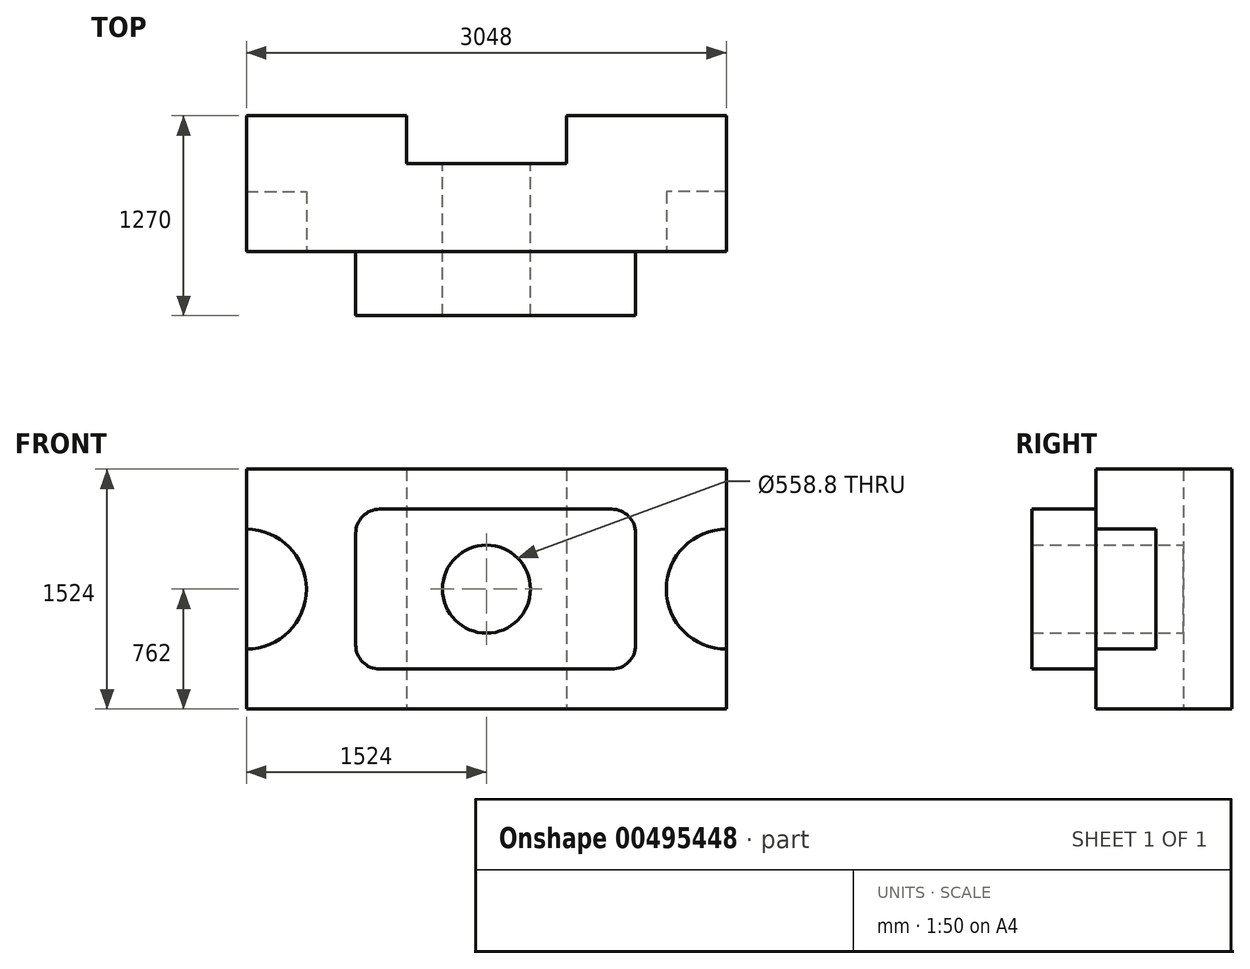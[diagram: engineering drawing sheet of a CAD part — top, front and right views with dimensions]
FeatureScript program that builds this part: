
annotation { "Feature Type Name" : "Feature", "Feature Type Description" : "" }
export const myFeature = defineFeature(function(context is Context, id is Id, definition is map)
    precondition{}
    {
        {
            var Q0;
            Q0=qCreatedBy(makeId("Front.planeOp"),FACE);
            var sketch = newSketch(context, id + "F0", { "sketchPlane" : qUnion([Q0])});
            skLineSegment(sketch, "E0.bottom", {"start": v(1524, -762) * mm, "end": v(-1524, -762) * mm});
            skLineSegment(sketch, "E0.top", {"start": v(1524, 762) * mm, "end": v(-1524, 762) * mm});
            skLineSegment(sketch, "E0.left", {"start": v(1524, -762) * mm, "end": v(1524, 762) * mm});
            skLineSegment(sketch, "E0.right", {"start": v(-1524, -762) * mm, "end": v(-1524, 762) * mm});
            skPoint(sketch, "E0.middle", {"position": v(0, 0) * mm});
            skSolve(sketch);
        }
        {
            var Q0;
            Q0=makeQuery(id+"F0.imprint","IMPRINT",FACE,{"disambiguationData":[TD([[makeQuery(id+"F0.imprint","IMPRINT",EDGE,{"derivedFrom":sQuery(id+"F0.wireOp",EDGE,"E0.bottom")}),-1.0]])]});
            extrude(context, id + "F1", {"entities" : qUnion([Q0]), "depth" : 863.6 * mm});
        }
        {
            var Q0;
            Q0=makeQuery(id+"F1.opExtrude","CAP_FACE",FACE,{"disambiguationData":[OSD([sQuery(id+"F0.wireOp",EDGE,"E0.bottom"),sQuery(id+"F0.wireOp",EDGE,"E0.top"),sQuery(id+"F0.wireOp",EDGE,"E0.left"),sQuery(id+"F0.wireOp",EDGE,"E0.right")])],"isStart":false});
            var sketch = newSketch(context, id + "F2", { "sketchPlane" : qUnion([Q0])});
            skArc(sketch, "E1", {"start": v(-1524, -381) * mm, "mid": v(-1143, 0) * mm, "end": v(-1524, 381) * mm});
            skArc(sketch, "E2", {"start": v(1524, 381) * mm, "mid": v(1143, 0) * mm, "end": v(1524, -381) * mm});
            skLineSegment(sketch, "E3", {"start": v(-1524, 381) * mm, "end": v(-1524, -381) * mm});
            skLineSegment(sketch, "E4", {"start": v(1524, 381) * mm, "end": v(1524, -381) * mm});
            skSolve(sketch);
        }
        {
            var Q0;
            Q0=makeQuery(id+"F2.imprint","IMPRINT",FACE,{"disambiguationData":[TD([[makeQuery(id+"F2.imprint","IMPRINT",EDGE,{"derivedFrom":sQuery(id+"F2.wireOp",EDGE,"E1")}),1.0]])]});
            var Q1;
            Q1=makeQuery(id+"F2.imprint","IMPRINT",FACE,{"disambiguationData":[TD([[makeQuery(id+"F2.imprint","IMPRINT",EDGE,{"derivedFrom":sQuery(id+"F2.wireOp",EDGE,"E2")}),1.0]])]});
            extrude(context, id + "F3", {"entities" : qUnion([Q0, Q1]), "operationType" : NewBodyOperationType.REMOVE, "oppositeDirection" : true, "depth" : 381 * mm});
        }
        {
            var Q0;
            Q0=makeQuery(id+"F1.opExtrude","SWEPT_FACE",FACE,{"disambiguationData":[OSD([sQuery(id+"F0.wireOp",EDGE,"E0.bottom")])]});
            var sketch = newSketch(context, id + "F4", { "sketchPlane" : qUnion([Q0])});
            skLineSegment(sketch, "E5.top", {"start": v(508, 304.8) * mm, "end": v(-508, 304.8) * mm});
            skLineSegment(sketch, "E5.left", {"start": v(508, 0) * mm, "end": v(508, 304.8) * mm});
            skLineSegment(sketch, "E5.right", {"start": v(-508, 0) * mm, "end": v(-508, 304.8) * mm});
            skPoint(sketch, "E5.middle", {"position": v(0, 0) * mm});
            skLineSegment(sketch, "E6", {"start": v(-508, 0) * mm, "end": v(508, 0) * mm});
            skPoint(sketch, "E5.bottom.end.orphan", {"position": v(-508, -304.8) * mm});
            skPoint(sketch, "E7.orphan", {"position": v(508, -304.8) * mm});
            skSolve(sketch);
        }
        {
            var Q0;
            Q0=makeQuery(id+"F4.imprint","IMPRINT",FACE,{"disambiguationData":[TD([[makeQuery(id+"F4.imprint","IMPRINT",EDGE,{"derivedFrom":sQuery(id+"F4.wireOp",EDGE,"E5.top")}),1.0]])]});
            extrude(context, id + "F5", {"entities" : qUnion([Q0]), "operationType" : NewBodyOperationType.REMOVE, "endBound" : BoundingType.THROUGH_ALL, "oppositeDirection" : true, "depth" : 25.4 * mm});
        }
        {
            var Q0;
            Q0=makeQuery(id+"F1.opExtrude","CAP_FACE",FACE,{"disambiguationData":[OSD([sQuery(id+"F0.wireOp",EDGE,"E0.bottom"),sQuery(id+"F0.wireOp",EDGE,"E0.top"),sQuery(id+"F0.wireOp",EDGE,"E0.left"),sQuery(id+"F0.wireOp",EDGE,"E0.right")])],"isStart":false});
            var sketch = newSketch(context, id + "F6", { "sketchPlane" : qUnion([Q0])});
            skLineSegment(sketch, "E8.bottom", {"start": v(795.49, 508) * mm, "end": v(-677.71, 508) * mm});
            skLineSegment(sketch, "E8.top", {"start": v(795.49, -508) * mm, "end": v(-677.71, -508) * mm});
            skLineSegment(sketch, "E8.left", {"start": v(947.89, 355.6) * mm, "end": v(947.89, -355.6) * mm});
            skLineSegment(sketch, "E8.right", {"start": v(-830.11, 355.6) * mm, "end": v(-830.11, -355.6) * mm});
            skPoint(sketch, "E8.middle", {"position": v(58.89, 0) * mm});
            skPoint(sketch, "E9.visualSharp", {"position": v(-830.11, 508) * mm});
            skArc(sketch, "E9.filletArc", {"start": v(-677.71, 508) * mm, "mid": v(-785.48, 463.36) * mm, "end": v(-830.11, 355.6) * mm});
            skPoint(sketch, "E10.visualSharp", {"position": v(947.89, 508) * mm});
            skArc(sketch, "E10.filletArc", {"start": v(947.89, 355.6) * mm, "mid": v(903.25, 463.36) * mm, "end": v(795.49, 508) * mm});
            skPoint(sketch, "E11.visualSharp", {"position": v(947.89, -508) * mm});
            skArc(sketch, "E11.filletArc", {"start": v(795.49, -508) * mm, "mid": v(903.25, -463.36) * mm, "end": v(947.89, -355.6) * mm});
            skPoint(sketch, "E12.visualSharp", {"position": v(-830.11, -508) * mm});
            skArc(sketch, "E12.filletArc", {"start": v(-830.11, -355.6) * mm, "mid": v(-785.48, -463.36) * mm, "end": v(-677.71, -508) * mm});
            skSolve(sketch);
        }
        {
            var Q0;
            Q0=makeQuery(id+"F6.imprint","IMPRINT",FACE,{"disambiguationData":[TD([[makeQuery(id+"F6.imprint","IMPRINT",EDGE,{"derivedFrom":sQuery(id+"F6.wireOp",EDGE,"E8.bottom")}),1.0]])]});
            extrude(context, id + "F7", {"entities" : qUnion([Q0]), "operationType" : NewBodyOperationType.ADD, "depth" : 406.4 * mm});
        }
        {
            var Q0;
            Q0=makeQuery(id+"F1.opExtrude","CAP_FACE",FACE,{"disambiguationData":[OSD([sQuery(id+"F0.wireOp",EDGE,"E0.bottom"),sQuery(id+"F0.wireOp",EDGE,"E0.top"),sQuery(id+"F0.wireOp",EDGE,"E0.left"),sQuery(id+"F0.wireOp",EDGE,"E0.right")])],"isStart":false});
            var sketch = newSketch(context, id + "F8", { "sketchPlane" : qUnion([Q0])});
            skCircle(sketch, "E13", {"center": v(0, 0) * mm, "radius": 279.4 * mm});
            skSolve(sketch);
        }
        {
            var Q0;
            Q0=qSketchRegion(id+"F8",true);
            extrude(context, id + "F9", {"entities" : qUnion([Q0]), "operationType" : NewBodyOperationType.REMOVE, "endBound" : BoundingType.THROUGH_ALL, "depth" : 25.4 * mm});
        }
        {
            var Q0;
            Q0=makeQuery(id+"F9.boolean.opBoolean","COPY",FACE,{"derivedFrom":makeQuery(id+"F9.opExtrude","CAP_FACE",FACE,{"disambiguationData":[OSD([sQuery(id+"F8.wireOp",EDGE,"E13")])],"isStart":true})});
            extrude(context, id + "F10", {"entities" : qUnion([Q0]), "operationType" : NewBodyOperationType.REMOVE, "endBound" : BoundingType.THROUGH_ALL, "oppositeDirection" : true, "depth" : 25.4 * mm});
        }
    });
